# Revit family: E_Cable Tray Support_MEPcontent_OBO Bettermann_I IS8 FT
name_source: partatom
category: Cable Tray Fittings
revit_build: Autodesk Revit MEP 2015 (Build: 20140606_1530(x64)
units: mm (PartAtom-declared; Revit-internal decimal feet)

## types (20) — shared parameters
Article Description = I support in fixed lengths.
Description = I support in fixed lengths.
EMCS Version = 2.0
ETIM Article Class = EC000386
Family Version = 10.14
Gray = Color RGB 189-187-185
IFCExportAs = IfcCableCarrierFittingType
IFCExportType = NOTDEFINED
MEPcontent Class = CABLE_TRAY_SUPPORT
Manufacturer = OBO BETTERMANN
Manufacturer URL = http://catalog4.obo-bettermann.com
Product Line = OBO BETTERMANN CableTrays
Revit Version = 2015
URL = www.stabiplan.com
Width 1 = 80 mm  [stored 0.262467 ft]
Width 2 = 42 mm  [stored 0.137795 ft]

## per-type parameters (varying)
| type | GTIN | Height 1 | Manufacturer Art. No. |
| IS 8 30 FT | 4012196182770 | 300 mm | 6337031 |
| IS 8 40 FT | 4012196182831 | 400 mm  [stored 1.31234 ft] | 6337058 |
| IS 8 50 FT | 4012196182893 | 500 mm  [stored 1.64042 ft] | 6337066 |
| IS 8 60 FT | 4012196182954 | 600 mm  [stored 1.9685 ft] | 6337074 |
| IS 8 70 FT | 4012196183012 | 700 mm  [stored 2.29659 ft] | 6337082 |
| IS 8 80 FT | 4012196183074 | 800 mm  [stored 2.62467 ft] | 6337090 |
| IS 8 90 FT | 4012196183135 | 900 mm  [stored 2.95276 ft] | 6337104 |
| IS 8 100 FT | 4012196183197 | 1000 mm  [stored 3.28084 ft] | 6337112 |
| IS 8 110 FT | 4012196183258 | 1100 mm | 6337120 |
| IS 8 120 FT | 4012195804550 | 1200 mm | 6337139 |
| IS 8 130 FT | 4012195805038 | 1300 mm  [stored 4.26509 ft] | 6337147 |
| IS 8 140 FT | 4012195934936 | 1400 mm  [stored 4.59318 ft] | 6337155 |
| IS 8 150 FT | 4012196183494 | 1500 mm  [stored 4.92126 ft] | 6337163 |
| IS 8 160 FT | 4012195934752 | 1600 mm  [stored 5.24934 ft] | 6337171 |
| IS 8 170 FT | 4012196183616 | 1700 mm  [stored 5.57743 ft] | 6337198 |
| IS 8 180 FT | 4012195934875 | 1800 mm  [stored 5.90551 ft] | 6337201 |
| IS 8 200 FT | 4012196183791 | 2000 mm  [stored 6.56168 ft] | 6337236 |
| IS 8 190 FT | 4012195934219 | 1900 mm  [stored 6.2336 ft] | 6337228 |
| IS 8 300 FT | 4012196183852 | 3000 mm  [stored 9.84252 ft] | 6337244 |
| IS 8 600 FT | 4012196183913 | 6000 mm  [stored 19.685 ft] | 6337252 |

note: column(s) folded — value = type name in every type: Article Type, Model

note: [stored X ft] marks values corroborated as IEEE doubles in the binary element streams (Revit-internal decimal feet)

## geometry (parser evidence)
native form markers: Blend x4, Sweep x2
no freeform markers — native parametric forms only
